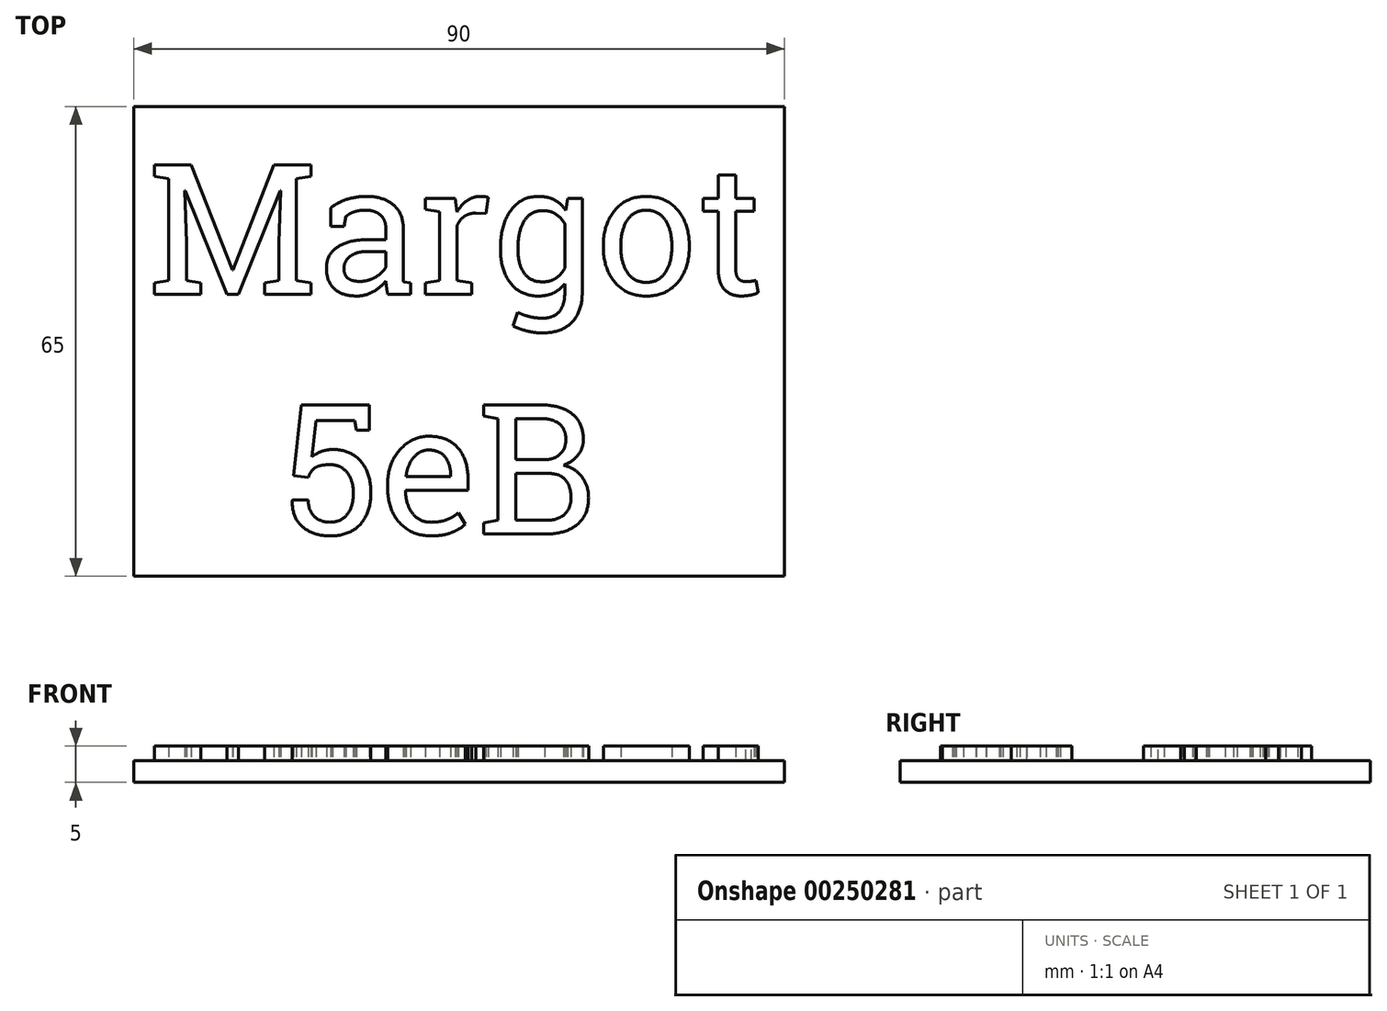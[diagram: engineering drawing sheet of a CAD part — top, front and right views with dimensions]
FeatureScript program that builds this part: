
annotation { "Feature Type Name" : "Feature", "Feature Type Description" : "" }
export const myFeature = defineFeature(function(context is Context, id is Id, definition is map)
    precondition{}
    {
        {
            var Q0;
            Q0=qCreatedBy(makeId("Top.planeOp"),FACE);
            var sketch = newSketch(context, id + "F0", { "sketchPlane" : qUnion([Q0])});
            skLineSegment(sketch, "E0.bottom", {"start": v(0, 15.85) * mm, "end": v(90, 15.85) * mm});
            skLineSegment(sketch, "E0.top", {"start": v(0, -49.15) * mm, "end": v(90, -49.15) * mm});
            skLineSegment(sketch, "E0.left", {"start": v(0, 15.85) * mm, "end": v(0, -49.15) * mm});
            skLineSegment(sketch, "E0.right", {"start": v(90, 15.85) * mm, "end": v(90, -49.15) * mm});
            skSolve(sketch);
        }
        {
            var Q0;
            Q0=makeQuery(id+"F0.imprint","IMPRINT",FACE,{"disambiguationData":[TD([[makeQuery(id+"F0.imprint","IMPRINT",EDGE,{"derivedFrom":sQuery(id+"F0.wireOp",EDGE,"E0.bottom")}),-1.0]])]});
            extrude(context, id + "F1", {"entities" : qUnion([Q0]), "depth" : 3 * mm});
        }
        {
            var Q0;
            Q0=makeQuery(id+"F1.opExtrude","CAP_FACE",FACE,{"disambiguationData":[OSD([sQuery(id+"F0.wireOp",EDGE,"E0.bottom"),sQuery(id+"F0.wireOp",EDGE,"E0.top"),sQuery(id+"F0.wireOp",EDGE,"E0.left"),sQuery(id+"F0.wireOp",EDGE,"E0.right")])],"isStart":false});
            var sketch = newSketch(context, id + "F2", { "sketchPlane" : qUnion([Q0])});
            skText(sketch, "E1", { "text": "Margot\n   5eB", "fontName": "RobotoSlab-Regular.ttf"});
            const initialGuessF2  = {"E1": [0.002, -0.01012, 1, 0, 0.0181]};
            skSetInitialGuess(sketch, initialGuessF2);
            skSolve(sketch);
        }
        {
            var Q0;
            Q0 = qSketchRegion(id + "F2", true);
            extrude(context, id + "F3", {"entities" : qUnion([Q0]), "operationType" : NewBodyOperationType.ADD, "depth" : 2 * mm});
        }
    });
